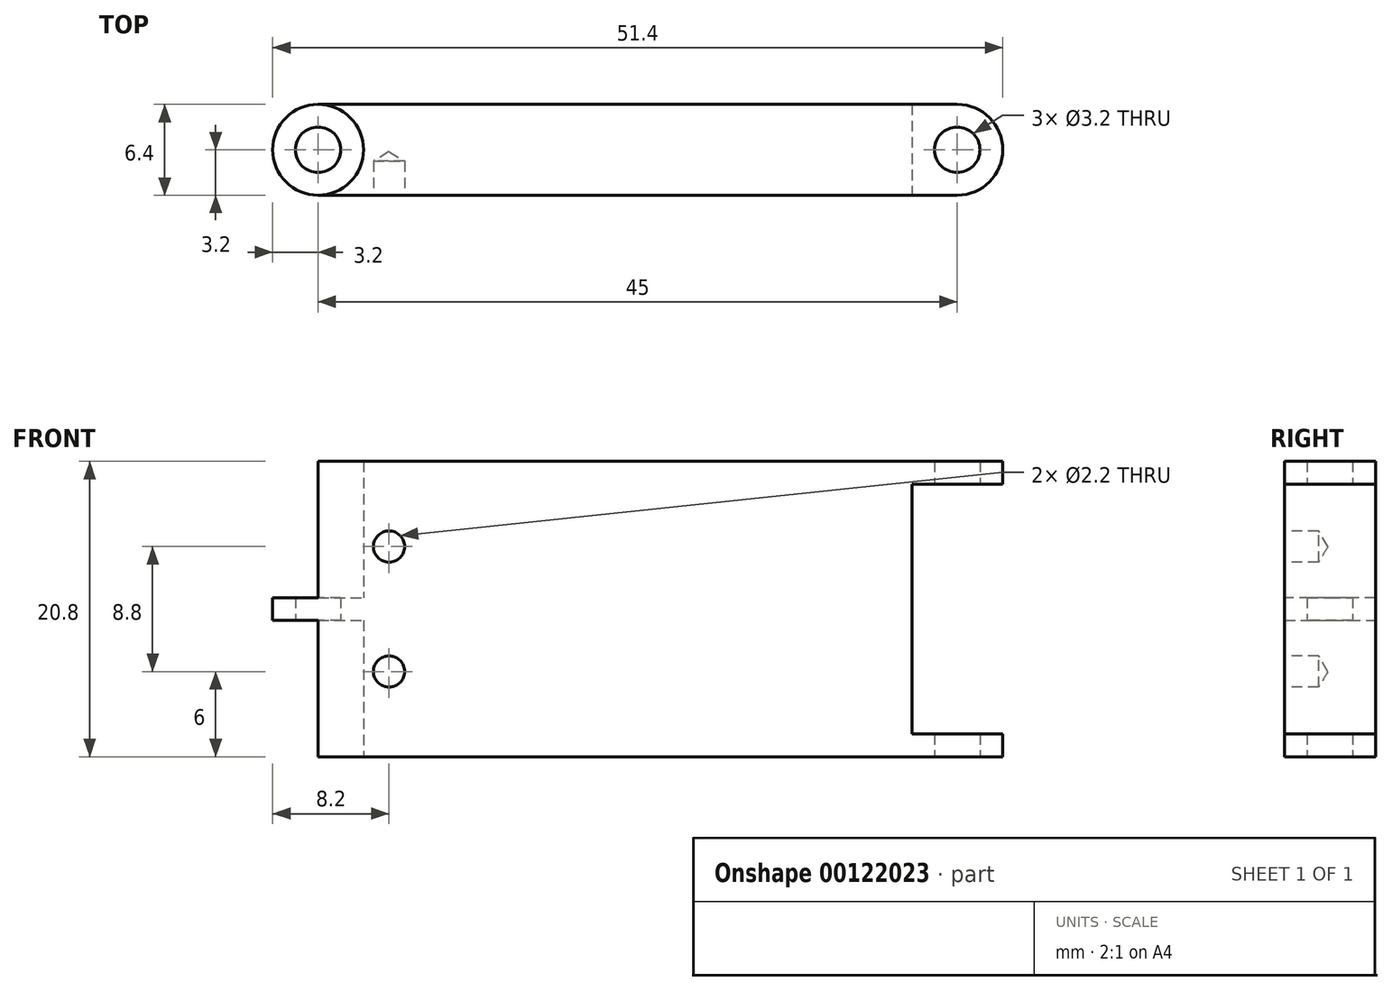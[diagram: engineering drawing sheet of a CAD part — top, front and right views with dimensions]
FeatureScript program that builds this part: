
annotation { "Feature Type Name" : "Feature", "Feature Type Description" : "" }
export const myFeature = defineFeature(function(context is Context, id is Id, definition is map)
    precondition{}
    {
        {
            var Q0;
            Q0=qCreatedBy(makeId("Top.planeOp"),FACE);
            var sketch = newSketch(context, id + "F0", { "sketchPlane" : qUnion([Q0])});
            skPoint(sketch, "E0", {"position": v(0, 0) * mm});
            skPoint(sketch, "E1", {"position": v(-22.5, 0) * mm});
            skPoint(sketch, "E2", {"position": v(22.5, 0) * mm});
            skCircle(sketch, "E3", {"center": v(-22.5, 0) * mm, "radius": 1.6 * mm});
            skCircle(sketch, "E4", {"center": v(22.5, 0) * mm, "radius": 1.6 * mm});
            skCircle(sketch, "E5.0", {"center": v(-22.5, 0) * mm, "radius": 3.2 * mm});
            skCircle(sketch, "E6.0", {"center": v(22.5, 0) * mm, "radius": 3.2 * mm});
            skPoint(sketch, "E7", {"position": v(-22.5, 3.2) * mm});
            skPoint(sketch, "E8", {"position": v(-22.5, -3.2) * mm});
            skPoint(sketch, "E9", {"position": v(22.5, -3.2) * mm});
            skPoint(sketch, "E10", {"position": v(22.5, 3.2) * mm});
            skLineSegment(sketch, "E11", {"start": v(-22.5, 3.2) * mm, "end": v(22.5, 3.2) * mm});
            skLineSegment(sketch, "E12", {"start": v(-22.5, -3.2) * mm, "end": v(22.5, -3.2) * mm});
            skPoint(sketch, "E13", {"position": v(-20.9, 0) * mm});
            skPoint(sketch, "E14", {"position": v(20.9, 0) * mm});
            skPoint(sketch, "E15", {"position": v(19.3, 0) * mm});
            skPoint(sketch, "E16", {"position": v(-19.3, 0) * mm});
            skLineSegment(sketch, "E17", {"start": v(-22.5, 3.2) * mm, "end": v(-22.5, 1.6) * mm});
            skLineSegment(sketch, "E18", {"start": v(-22.5, -3.2) * mm, "end": v(-22.5, -1.6) * mm});
            skLineSegment(sketch, "E19", {"start": v(19.3, 0) * mm, "end": v(19.3, 3.2) * mm});
            skLineSegment(sketch, "E20", {"start": v(19.3, 0) * mm, "end": v(19.3, -3.2) * mm});
            skSolve(sketch);
        }
        {
            var Q0;
            {var subQ0=sQuery(id+"F0.wireOp",EDGE,"E19");Q0=makeQuery(id+"F0.imprint","IMPRINT",FACE,{"disambiguationData":[TD([[makeQuery(id+"F0.imprint","IMPRINT",EDGE,{"derivedFrom":subQ0}),1.0]])]});}
            var Q1;
            {var subQ3=sQuery(id+"F0.wireOp",EDGE,"E19");Q1=makeQuery(id+"F0.imprint","IMPRINT",FACE,{"disambiguationData":[TD([[makeQuery(id+"F0.imprint","IMPRINT",EDGE,{"derivedFrom":subQ3}),-1.0]])]});}
            var Q2;
            Q2=makeQuery(id+"F0.imprint","IMPRINT",FACE,{"disambiguationData":[TD([[makeQuery(id+"F0.imprint","IMPRINT",EDGE,{"derivedFrom":sQuery(id+"F0.wireOp",EDGE,"E4")}),-1.0]])]});
            var Q3;
            {var subQ3=sQuery(id+"F0.wireOp",EDGE,"E20");Q3=makeQuery(id+"F0.imprint","IMPRINT",FACE,{"disambiguationData":[TD([[makeQuery(id+"F0.imprint","IMPRINT",EDGE,{"derivedFrom":subQ3}),1.0]])]});}
            extrude(context, id + "F1", {"entities" : qUnion([Q0, Q1, Q2, Q3]), "depth" : 1.6 * mm});
        }
        {
            var Q0;
            Q0=makeQuery(id+"F1.opExtrude","CAP_FACE",FACE,{"disambiguationData":[OSD([sQuery(id+"F0.wireOp",EDGE,"E4"),sQuery(id+"F0.wireOp",EDGE,"E5.0"),sQuery(id+"F0.wireOp",EDGE,"E6.0"),sQuery(id+"F0.wireOp",EDGE,"E11"),sQuery(id+"F0.wireOp",EDGE,"E12")])],"isStart":false});
            cPlane(context, id + "F2", {"entities" : qUnion([Q0]), "cplaneType" : CPlaneType.OFFSET, "offset" : 0 * mm, "width" : 150 * mm, "height" : 150 * mm});
        }
        {
            var Q0;
            Q0=qCreatedBy(id+"F2.planeOp",FACE);
            var sketch = newSketch(context, id + "F3", { "sketchPlane" : qUnion([Q0])});
            skCircle(sketch, "E21.0", {"center": v(-22.5, 0) * mm, "radius": 3.2 * mm});
            skCircle(sketch, "E21.1", {"center": v(22.5, 0) * mm, "radius": 3.2 * mm});
            skLineSegment(sketch, "E21.2", {"start": v(-22.5, 3.2) * mm, "end": v(22.5, 3.2) * mm});
            skLineSegment(sketch, "E21.3", {"start": v(-22.5, -3.2) * mm, "end": v(22.5, -3.2) * mm});
            skCircle(sketch, "E21.4", {"center": v(22.5, 0) * mm, "radius": 1.6 * mm});
            skCircle(sketch, "E21.5", {"center": v(-22.5, 0) * mm, "radius": 1.6 * mm});
            skLineSegment(sketch, "E21.6", {"start": v(19.3, 0) * mm, "end": v(19.3, 3.2) * mm});
            skLineSegment(sketch, "E21.7", {"start": v(19.3, 0) * mm, "end": v(19.3, -3.2) * mm});
            skLineSegment(sketch, "E21.8", {"start": v(-22.5, 3.2) * mm, "end": v(-22.5, 1.6) * mm});
            skLineSegment(sketch, "E21.9", {"start": v(-22.5, -3.2) * mm, "end": v(-22.5, -1.6) * mm});
            skArc(sketch, "E21.10", {"start": v(-22.5, -3.2) * mm, "mid": v(-19.3, 0) * mm, "end": v(-22.5, 3.2) * mm});
            skArc(sketch, "E21.11", {"start": v(22.5, -3.2) * mm, "mid": v(25.7, 0) * mm, "end": v(22.5, 3.2) * mm});
            skCircle(sketch, "E21.12", {"center": v(22.5, 0) * mm, "radius": 1.6 * mm});
            skLineSegment(sketch, "E21.14", {"start": v(-22.5, -3.2) * mm, "end": v(22.5, -3.2) * mm});
            skArc(sketch, "E21.15", {"start": v(22.5, -3.2) * mm, "mid": v(25.7, 0) * mm, "end": v(22.5, 3.2) * mm});
            skLineSegment(sketch, "E21.16", {"start": v(-22.5, 3.2) * mm, "end": v(22.5, 3.2) * mm});
            skArc(sketch, "E21.18", {"start": v(-22.5, -3.2) * mm, "mid": v(-19.3, 0) * mm, "end": v(-22.5, 3.2) * mm});
            skLineSegment(sketch, "E21.20", {"start": v(-22.5, 3.2) * mm, "end": v(22.5, 3.2) * mm});
            skCircle(sketch, "E21.22", {"center": v(22.5, 0) * mm, "radius": 1.6 * mm});
            skLineSegment(sketch, "E21.23", {"start": v(-22.5, -3.2) * mm, "end": v(22.5, -3.2) * mm});
            skPoint(sketch, "E22", {"position": v(-25.7, 0) * mm});
            skPoint(sketch, "E23", {"position": v(25.7, 0) * mm});
            skLineSegment(sketch, "E24", {"start": v(-25.7, 0) * mm, "end": v(-25.7, -3.2) * mm, "construction": true});
            skSolve(sketch);
        }
        {
            var Q0;
            {var subQ1=sQuery(id+"F3.wireOp",EDGE,"E21.6");Q0=makeQuery(id+"F3.imprint","IMPRINT",FACE,{"disambiguationData":[TD([[makeQuery(id+"F3.imprint","IMPRINT",EDGE,{"derivedFrom":subQ1}),1.0]])]});}
            extrude(context, id + "F4", {"entities" : qUnion([Q0]), "operationType" : NewBodyOperationType.ADD, "depth" : 8 * mm});
        }
        {
            var Q0;
            Q0=makeQuery(id+"F4.opExtrude","CAP_FACE",FACE,{"disambiguationData":[OSD([sQuery(id+"F3.wireOp",EDGE,"E21.0"),sQuery(id+"F3.wireOp",EDGE,"E21.6"),sQuery(id+"F3.wireOp",EDGE,"E21.7"),sQuery(id+"F3.wireOp",EDGE,"E21.20"),sQuery(id+"F3.wireOp",EDGE,"E21.23")])],"isStart":false});
            var sketch = newSketch(context, id + "F5", { "sketchPlane" : qUnion([Q0])});
            skLineSegment(sketch, "E25.0.0", {"start": v(19.3, -3.2) * mm, "end": v(19.3, 3.2) * mm});
            skLineSegment(sketch, "E25.0.1", {"start": v(19.3, 3.2) * mm, "end": v(-22.5, 3.2) * mm});
            skArc(sketch, "E25.0.2", {"start": v(-22.5, 3.2) * mm, "mid": v(-19.3, 0) * mm, "end": v(-22.5, -3.2) * mm});
            skLineSegment(sketch, "E25.0.3", {"start": v(-22.5, -3.2) * mm, "end": v(19.3, -3.2) * mm});
            skCircle(sketch, "E26.0", {"center": v(-22.5, 0) * mm, "radius": 1.6 * mm});
            skCircle(sketch, "E27.0", {"center": v(-22.5, 0) * mm, "radius": 3.2 * mm});
            skSolve(sketch);
        }
        {
            var Q0;
            Q0=makeQuery(id+"F5.imprint","IMPRINT",FACE,{"disambiguationData":[TD([[makeQuery(id+"F5.imprint","IMPRINT",EDGE,{"derivedFrom":sQuery(id+"F5.wireOp",EDGE,"E25.0.0")}),-1.0]])]});
            var Q1;
            Q1=makeQuery(id+"F5.imprint","IMPRINT",FACE,{"disambiguationData":[TD([[makeQuery(id+"F5.imprint","IMPRINT",EDGE,{"derivedFrom":sQuery(id+"F5.wireOp",EDGE,"E26.0")}),-1.0]])]});
            extrude(context, id + "F6", {"entities" : qUnion([Q0, Q1]), "operationType" : NewBodyOperationType.ADD, "depth" : 1.6 * mm});
        }
        {
            var Q0;
            Q0=makeQuery(id+"F6.opExtrude","CAP_FACE",FACE,{"disambiguationData":[OSD([sQuery(id+"F5.wireOp",EDGE,"E25.0.0"),sQuery(id+"F5.wireOp",EDGE,"E25.0.1"),sQuery(id+"F5.wireOp",EDGE,"E25.0.3"),sQuery(id+"F5.wireOp",EDGE,"E26.0"),sQuery(id+"F5.wireOp",EDGE,"E27.0")])],"isStart":false});
            var sketch = newSketch(context, id + "F7", { "sketchPlane" : qUnion([Q0])});
            skLineSegment(sketch, "E28.0.0", {"start": v(19.3, -3.2) * mm, "end": v(19.3, 3.2) * mm});
            skLineSegment(sketch, "E28.0.1", {"start": v(19.3, 3.2) * mm, "end": v(-22.5, 3.2) * mm});
            skArc(sketch, "E28.0.2", {"start": v(-22.5, 3.2) * mm, "mid": v(-25.7, 0) * mm, "end": v(-22.5, -3.2) * mm});
            skLineSegment(sketch, "E28.0.3", {"start": v(-22.5, -3.2) * mm, "end": v(19.3, -3.2) * mm});
            skCircle(sketch, "E29.0", {"center": v(-22.5, 0) * mm, "radius": 3.2 * mm});
            skLineSegment(sketch, "E30.0", {"start": v(-22.5, 3.2) * mm, "end": v(22.5, 3.2) * mm});
            skLineSegment(sketch, "E31.0", {"start": v(-22.5, -3.2) * mm, "end": v(22.5, -3.2) * mm});
            skCircle(sketch, "E32.0", {"center": v(22.5, 0) * mm, "radius": 3.2 * mm});
            skCircle(sketch, "E33.0", {"center": v(22.5, 0) * mm, "radius": 1.6 * mm});
            skLineSegment(sketch, "E34.0", {"start": v(-22.5, 3.2) * mm, "end": v(-22.5, 1.6) * mm});
            skLineSegment(sketch, "E35.0", {"start": v(-22.5, -3.2) * mm, "end": v(-22.5, -1.6) * mm});
            skSolve(sketch);
        }
        {
            var Q0;
            {var subQ0=sQuery(id+"F7.wireOp",EDGE,"E30.0");var subQ1=sQuery(id+"F7.wireOp",EDGE,"E28.0.0");var subQ2=makeQuery(id+"F7.imprint","INTERSECT",VERTEX,{"derivedFrom":[subQ1,subQ0]});Q0=makeQuery(id+"F7.imprint","IMPRINT",FACE,{"disambiguationData":[TD([[makeQuery(id+"F7.imprint","IMPRINT",EDGE,{"disambiguationData":[TD([[subQ2,-1.0]])],"derivedFrom":subQ1}),-1.0]])]});}
            extrude(context, id + "F8", {"entities" : qUnion([Q0]), "operationType" : NewBodyOperationType.ADD, "depth" : 8 * mm});
        }
        {
            var Q0;
            Q0=makeQuery(id+"F8.opExtrude","CAP_FACE",FACE,{"disambiguationData":[OSD([sQuery(id+"F7.wireOp",EDGE,"E28.0.0"),sQuery(id+"F7.wireOp",EDGE,"E29.0"),sQuery(id+"F7.wireOp",EDGE,"E30.0"),sQuery(id+"F7.wireOp",EDGE,"E31.0")])],"isStart":false});
            var sketch = newSketch(context, id + "F9", { "sketchPlane" : qUnion([Q0])});
            skCircle(sketch, "E36.0", {"center": v(22.5, 0) * mm, "radius": 3.2 * mm});
            skLineSegment(sketch, "E37.0", {"start": v(-22.5, 3.2) * mm, "end": v(22.5, 3.2) * mm});
            skLineSegment(sketch, "E38.0", {"start": v(-22.5, -3.2) * mm, "end": v(22.5, -3.2) * mm});
            skCircle(sketch, "E39.0", {"center": v(22.5, 0) * mm, "radius": 1.6 * mm});
            skSolve(sketch);
        }
        {
            var Q0;
            {var subQ6=makeQuery(id+"F8.opExtrude","CAP_EDGE",EDGE,{"disambiguationData":[OSD([sQuery(id+"F7.wireOp",EDGE,"E29.0")])],"isStart":false});Q0=makeQuery(id+"F9.imprint","IMPRINT",FACE,{"disambiguationData":[TD([[makeQuery(id+"F9.imprint","IMPRINT",EDGE,{"derivedFrom":subQ6}),-1.0]])]});}
            var Q1;
            {var subQ0=sQuery(id+"F9.wireOp",EDGE,"E37.0");var subQ1=sQuery(id+"F9.wireOp",EDGE,"E36.0");var subQ2=makeQuery(id+"F9.imprint","INTERSECT",VERTEX,{"derivedFrom":[subQ1,subQ0]});Q1=makeQuery(id+"F9.imprint","IMPRINT",FACE,{"disambiguationData":[TD([[makeQuery(id+"F9.imprint","IMPRINT",EDGE,{"disambiguationData":[TD([[subQ2,-1.0]])],"derivedFrom":subQ1}),-1.0]])]});}
            var Q2;
            {var subQ0=sQuery(id+"F9.wireOp",EDGE,"E36.0");var subQ1=makeQuery(id+"F9.imprint","INTERSECT",VERTEX,{"derivedFrom":[subQ0,sQuery(id+"F9.wireOp",EDGE,"E37.0")]});Q2=makeQuery(id+"F9.imprint","IMPRINT",FACE,{"disambiguationData":[TD([[makeQuery(id+"F9.imprint","IMPRINT",EDGE,{"disambiguationData":[TD([[subQ1,-1.0]])],"derivedFrom":subQ0}),1.0]])]});}
            var Q3;
            {var subQ0=sQuery(id+"F9.wireOp",EDGE,"E38.0");var subQ1=sQuery(id+"F9.wireOp",EDGE,"E36.0");var subQ2=makeQuery(id+"F9.imprint","INTERSECT",VERTEX,{"derivedFrom":[subQ1,subQ0]});Q3=makeQuery(id+"F9.imprint","IMPRINT",FACE,{"disambiguationData":[TD([[makeQuery(id+"F9.imprint","IMPRINT",EDGE,{"disambiguationData":[TD([[subQ2,1.0]])],"derivedFrom":subQ1}),-1.0]])]});}
            extrude(context, id + "F10", {"entities" : qUnion([Q0, Q1, Q2, Q3]), "operationType" : NewBodyOperationType.ADD, "depth" : 1.6 * mm});
        }
        {
            var Q0;
            Q0=makeQuery(id+"F10.boolean.opBoolean","MERGE",FACE,{"derivedFrom":[makeQuery(id+"F8.boolean.opBoolean","MERGE",FACE,{"derivedFrom":[makeQuery(id+"F6.boolean.opBoolean","MERGE",FACE,{"derivedFrom":[makeQuery(id+"F4.boolean.opBoolean","MERGE",FACE,{"derivedFrom":[makeQuery(id+"F1.opExtrude","SWEPT_FACE",FACE,{"disambiguationData":[OSD([sQuery(id+"F0.wireOp",EDGE,"E12")])]}),makeQuery(id+"F4.opExtrude","SWEPT_FACE",FACE,{"disambiguationData":[OSD([sQuery(id+"F3.wireOp",EDGE,"E21.23")])]})]}),makeQuery(id+"F6.opExtrude","SWEPT_FACE",FACE,{"disambiguationData":[OSD([sQuery(id+"F5.wireOp",EDGE,"E25.0.3")])]})]}),makeQuery(id+"F8.opExtrude","SWEPT_FACE",FACE,{"disambiguationData":[OSD([sQuery(id+"F7.wireOp",EDGE,"E31.0")])]})]}),makeQuery(id+"F10.opExtrude","SWEPT_FACE",FACE,{"disambiguationData":[OSD([sQuery(id+"F9.wireOp",EDGE,"E38.0")])]})]});
            var sketch = newSketch(context, id + "F11", { "sketchPlane" : qUnion([Q0])});
            skLineSegment(sketch, "E40", {"start": v(22.5, 1.6) * mm, "end": v(22.5, 0) * mm});
            skLineSegment(sketch, "E41", {"start": v(19.3, 1.6) * mm, "end": v(22.5, 1.6) * mm});
            skLineSegment(sketch, "E42", {"start": v(19.3, 19.2) * mm, "end": v(19.3, 1.6) * mm});
            skLineSegment(sketch, "E43", {"start": v(19.3, 19.2) * mm, "end": v(22.5, 19.2) * mm});
            skLineSegment(sketch, "E44", {"start": v(22.5, 20.8) * mm, "end": v(22.5, 19.2) * mm});
            skLineSegment(sketch, "E45", {"start": v(-22.5, 20.8) * mm, "end": v(22.5, 20.8) * mm});
            skLineSegment(sketch, "E46", {"start": v(-22.5, 20.8) * mm, "end": v(-22.5, 11.2) * mm});
            skLineSegment(sketch, "E47", {"start": v(-22.5, 11.2) * mm, "end": v(-22.5, 9.6) * mm});
            skLineSegment(sketch, "E48", {"start": v(-22.5, 9.6) * mm, "end": v(-22.5, 0) * mm});
            skLineSegment(sketch, "E49", {"start": v(-22.5, 0) * mm, "end": v(22.5, 0) * mm});
            skPoint(sketch, "E50", {"position": v(-17.5, 20.8) * mm});
            skPoint(sketch, "E51", {"position": v(-17.5, 0) * mm});
            skCircle(sketch, "E52", {"center": v(-17.5, 14.8) * mm, "radius": 1.1 * mm});
            skCircle(sketch, "E53", {"center": v(-17.5, 6) * mm, "radius": 1.1 * mm});
            skSolve(sketch);
        }
        {
            var Q0;
            Q0=sQuery(id+"F11.wireOp",VERTEX,"E52.center");
            var Q1;
            Q1=sQuery(id+"F11.wireOp",VERTEX,"E53.center");
            var Q2;
            Q2=makeQuery(id+"F1.opExtrude","SWEPT_BODY",BODY,{"disambiguationData":[OSD([sQuery(id+"F0.wireOp",EDGE,"E4"),sQuery(id+"F0.wireOp",EDGE,"E5.0"),sQuery(id+"F0.wireOp",EDGE,"E6.0"),sQuery(id+"F0.wireOp",EDGE,"E11"),sQuery(id+"F0.wireOp",EDGE,"E12")])]});
            hole(context, id + "F12", {"style" : HoleStyle.SIMPLE, "endStyle" : HoleEndStyle.BLIND, "holeDiameter" : 2.2 * mm, "holeDepth" : 2.4 * mm, "locations" : qUnion([Q0, Q1]), "scope" : qUnion([Q2])});
        }
    });
